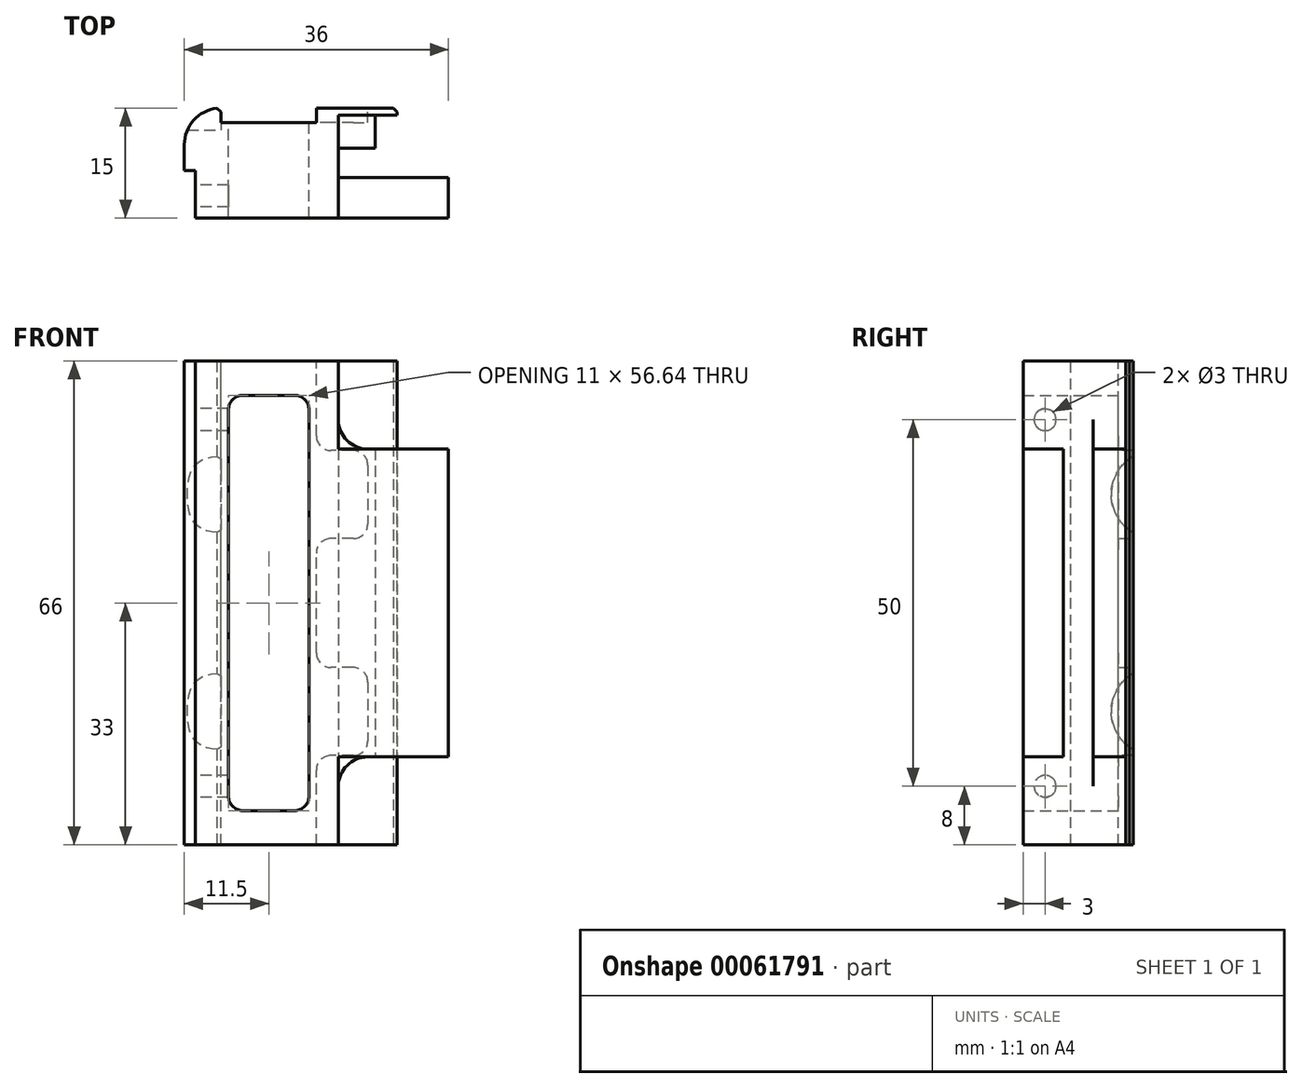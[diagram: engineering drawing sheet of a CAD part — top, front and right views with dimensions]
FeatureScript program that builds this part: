
annotation { "Feature Type Name" : "Feature", "Feature Type Description" : "" }
export const myFeature = defineFeature(function(context is Context, id is Id, definition is map)
    precondition{}
    {
        {
            var Q0;
            Q0=qCreatedBy(makeId("Front.planeOp"),FACE);
            var sketch = newSketch(context, id + "F0", { "sketchPlane" : qUnion([Q0])});
            skLineSegment(sketch, "E0.bottom", {"start": v(5.5, -28.32) * mm, "end": v(-5.5, -28.32) * mm});
            skLineSegment(sketch, "E0.top", {"start": v(5.5, 28.32) * mm, "end": v(-5.5, 28.32) * mm});
            skLineSegment(sketch, "E0.left", {"start": v(5.5, -28.32) * mm, "end": v(5.5, 28.32) * mm});
            skLineSegment(sketch, "E0.right", {"start": v(-5.5, -28.32) * mm, "end": v(-5.5, 28.32) * mm});
            skPoint(sketch, "E0.middle", {"position": v(0, 0) * mm});
            skLineSegment(sketch, "E1.bottom", {"start": v(9.5, -33) * mm, "end": v(-11.5, -33) * mm});
            skLineSegment(sketch, "E1.top", {"start": v(9.5, 33) * mm, "end": v(-11.5, 33) * mm});
            skLineSegment(sketch, "E1.right", {"start": v(-11.5, -33) * mm, "end": v(-11.5, 33) * mm});
            skLineSegment(sketch, "E2", {"start": v(9.5, 33) * mm, "end": v(9.5, -33) * mm});
            skSolve(sketch);
        }
        {
            var Q0;
            Q0 = qSketchRegion(id + "F0", true);
            extrude(context, id + "F1", {"entities" : qUnion([Q0]), "depth" : 15 * mm});
        }
        {
            var Q0;
            Q0=makeQuery(id+"F1.opExtrude","CAP_EDGE",EDGE,{"disambiguationData":[OSD([sQuery(id+"F0.wireOp",EDGE,"E1.right")])],"isStart":true});
            fillet(context, id + "F2", {"entities" : qUnion([Q0]), "radius" : 5 * mm, "tangentPropagation" : true, "allowEdgeOverflow" : false});
        }
        {
            var Q0;
            Q0=qCreatedBy(makeId("Front.planeOp"),FACE);
            var sketch = newSketch(context, id + "F3", { "sketchPlane" : qUnion([Q0])});
            skLineSegment(sketch, "E3.bottom", {"start": v(9.5, -21) * mm, "end": v(24.5, -21) * mm});
            skLineSegment(sketch, "E3.top", {"start": v(9.5, 21) * mm, "end": v(24.5, 21) * mm});
            skLineSegment(sketch, "E3.left", {"start": v(9.5, -21) * mm, "end": v(9.5, 21) * mm});
            skLineSegment(sketch, "E3.right", {"start": v(24.5, -21) * mm, "end": v(24.5, 21) * mm});
            skPoint(sketch, "E3.middle", {"position": v(17, 0) * mm});
            skSolve(sketch);
        }
        {
            var Q0;
            Q0=makeQuery(id+"F3.imprint","IMPRINT",FACE,{"disambiguationData":[TD([[makeQuery(id+"F3.imprint","IMPRINT",EDGE,{"derivedFrom":sQuery(id+"F3.wireOp",EDGE,"E3.bottom")}),1.0]])]});
            extrude(context, id + "F4", {"entities" : qUnion([Q0]), "operationType" : NewBodyOperationType.ADD, "depth" : 15 * mm, "hasSecondDirection" : true, "secondDirectionOppositeDirection" : false, "secondDirectionDepth" : 9.5 * mm});
        }
        {
            var Q0;
            Q0=makeQuery(id+"F1.opExtrude","SWEPT_EDGE",EDGE,{"disambiguationData":[OSD([sQuery(id+"F0.wireOp",EDGE,"E0.bottom"),sQuery(id+"F0.wireOp",EDGE,"E0.left")])]});
            var Q1;
            Q1=makeQuery(id+"F1.opExtrude","SWEPT_EDGE",EDGE,{"disambiguationData":[OSD([sQuery(id+"F0.wireOp",EDGE,"E0.bottom"),sQuery(id+"F0.wireOp",EDGE,"E0.right")])]});
            var Q2;
            Q2=makeQuery(id+"F1.opExtrude","SWEPT_EDGE",EDGE,{"disambiguationData":[OSD([sQuery(id+"F0.wireOp",EDGE,"E0.top"),sQuery(id+"F0.wireOp",EDGE,"E0.right")])]});
            var Q3;
            Q3=makeQuery(id+"F1.opExtrude","SWEPT_EDGE",EDGE,{"disambiguationData":[OSD([sQuery(id+"F0.wireOp",EDGE,"E0.top"),sQuery(id+"F0.wireOp",EDGE,"E0.left")])]});
            fillet(context, id + "F5", {"entities" : qUnion([Q0, Q1, Q2, Q3]), "radius" : 2 * mm, "tangentPropagation" : true, "allowEdgeOverflow" : false});
        }
        {
            var Q0;
            Q0=qCreatedBy(makeId("Top.planeOp"),FACE);
            var sketch = newSketch(context, id + "F6", { "sketchPlane" : qUnion([Q0])});
            skLineSegment(sketch, "E4.bottom", {"start": v(-10, -15) * mm, "end": v(-11.5, -15) * mm});
            skLineSegment(sketch, "E4.top", {"start": v(-10, -8.5) * mm, "end": v(-11.5, -8.5) * mm});
            skLineSegment(sketch, "E4.left", {"start": v(-10, -15) * mm, "end": v(-10, -8.5) * mm});
            skLineSegment(sketch, "E4.right", {"start": v(-11.5, -15) * mm, "end": v(-11.5, -8.5) * mm});
            skSolve(sketch);
        }
        {
            var Q0;
            Q0 = qSketchRegion(id + "F6", true);
            extrude(context, id + "F7", {"entities" : qUnion([Q0]), "operationType" : NewBodyOperationType.REMOVE, "oppositeDirection" : true, "depth" : 50 * mm, "hasSecondDirection" : true, "secondDirectionOppositeDirection" : false, "secondDirectionDepth" : 50 * mm});
        }
        {
            var Q0;
            Q0=makeQuery(id+"F7.boolean.opBoolean","COPY",FACE,{"derivedFrom":makeQuery(id+"F7.opExtrude","SWEPT_FACE",FACE,{"disambiguationData":[OSD([sQuery(id+"F6.wireOp",EDGE,"E4.left")])]})});
            var sketch = newSketch(context, id + "F8", { "sketchPlane" : qUnion([Q0])});
            skCircle(sketch, "E5", {"center": v(12, 25) * mm, "radius": 1.5 * mm});
            skCircle(sketch, "E6", {"center": v(12, -25) * mm, "radius": 1.5 * mm});
            skSolve(sketch);
        }
        {
            var Q0;
            Q0 = qSketchRegion(id + "F8", true);
            extrude(context, id + "F9", {"entities" : qUnion([Q0]), "operationType" : NewBodyOperationType.REMOVE, "oppositeDirection" : true, "depth" : 5 * mm});
        }
        {
            var Q0;
            Q0=qCreatedBy(makeId("Top.planeOp"),FACE);
            var sketch = newSketch(context, id + "F10", { "sketchPlane" : qUnion([Q0])});
            skLineSegment(sketch, "E7.bottom", {"start": v(17.5, -1) * mm, "end": v(14.5, -1) * mm});
            skLineSegment(sketch, "E7.top", {"start": v(17.5, 0) * mm, "end": v(14.5, 0) * mm});
            skLineSegment(sketch, "E7.left", {"start": v(17.5, -1) * mm, "end": v(17.5, 0) * mm});
            skLineSegment(sketch, "E7.right", {"start": v(14.5, -1) * mm, "end": v(14.5, 0) * mm});
            skLineSegment(sketch, "E8.bottom", {"start": v(9.5, 0) * mm, "end": v(14.5, 0) * mm});
            skLineSegment(sketch, "E8.top", {"start": v(9.5, -5.45) * mm, "end": v(14.5, -5.45) * mm});
            skLineSegment(sketch, "E8.left", {"start": v(9.5, 0) * mm, "end": v(9.5, -5.45) * mm});
            skLineSegment(sketch, "E8.right", {"start": v(14.5, 0) * mm, "end": v(14.5, -5.45) * mm});
            skSolve(sketch);
        }
        {
            var Q0;
            Q0=makeQuery(id+"F10.imprint","IMPRINT",FACE,{"disambiguationData":[TD([[makeQuery(id+"F10.imprint","IMPRINT",EDGE,{"derivedFrom":sQuery(id+"F10.wireOp",EDGE,"E7.bottom")}),-1.0]])]});
            var Q1;
            {var subQ2=sQuery(id+"F10.wireOp",EDGE,"E8.bottom");Q1=makeQuery(id+"F10.imprint","IMPRINT",FACE,{"disambiguationData":[TD([[makeQuery(id+"F10.imprint","IMPRINT",EDGE,{"derivedFrom":subQ2}),-1.0]])]});}
            extrude(context, id + "F11", {"entities" : qUnion([Q0, Q1]), "operationType" : NewBodyOperationType.ADD, "depth" : 33 * mm, "hasSecondDirection" : true, "secondDirectionOppositeDirection" : true, "secondDirectionDepth" : 33 * mm});
        }
        {
            var Q0;
            Q0=makeQuery(id+"F11.opExtrude","SWEPT_EDGE",EDGE,{"disambiguationData":[OSD([sQuery(id+"F10.wireOp",EDGE,"E7.top"),sQuery(id+"F10.wireOp",EDGE,"E7.left")])]});
            chamfer(context, id + "F12", {"entities" : qUnion([Q0]), "width" : 0.5 * mm, "tangentPropagation" : true});
        }
        {
            var Q0;
            Q0=makeQuery(id+"F4.boolean.opBoolean","MERGE",FACE,{"derivedFrom":[makeQuery(id+"F1.opExtrude","CAP_FACE",FACE,{"disambiguationData":[OSD([sQuery(id+"F0.wireOp",EDGE,"E0.bottom"),sQuery(id+"F0.wireOp",EDGE,"E0.top"),sQuery(id+"F0.wireOp",EDGE,"E0.left"),sQuery(id+"F0.wireOp",EDGE,"E0.right"),sQuery(id+"F0.wireOp",EDGE,"E1.bottom"),sQuery(id+"F0.wireOp",EDGE,"E1.top"),sQuery(id+"F0.wireOp",EDGE,"E1.right"),sQuery(id+"F0.wireOp",EDGE,"E2")])],"isStart":false}),makeQuery(id+"F4.opExtrude","CAP_FACE",FACE,{"disambiguationData":[OSD([sQuery(id+"F3.wireOp",EDGE,"E3.bottom"),sQuery(id+"F3.wireOp",EDGE,"E3.top"),sQuery(id+"F3.wireOp",EDGE,"E3.left"),sQuery(id+"F3.wireOp",EDGE,"E3.right")])],"isStart":false})]});
            var sketch = newSketch(context, id + "F13", { "sketchPlane" : qUnion([Q0])});
            skLineSegment(sketch, "E9.bottom", {"start": v(9.5, -33) * mm, "end": v(14.5, -33) * mm});
            skLineSegment(sketch, "E9.top", {"start": v(9.5, -21) * mm, "end": v(14.5, -21) * mm});
            skLineSegment(sketch, "E9.left", {"start": v(9.5, -33) * mm, "end": v(9.5, -21) * mm});
            skLineSegment(sketch, "E9.right", {"start": v(14.5, -33) * mm, "end": v(14.5, -21) * mm});
            skLineSegment(sketch, "E10.bottom", {"start": v(9.5, 33) * mm, "end": v(14.5, 33) * mm});
            skLineSegment(sketch, "E10.top", {"start": v(9.5, 21) * mm, "end": v(14.5, 21) * mm});
            skLineSegment(sketch, "E10.left", {"start": v(9.5, 33) * mm, "end": v(9.5, 21) * mm});
            skLineSegment(sketch, "E10.right", {"start": v(14.5, 33) * mm, "end": v(14.5, 21) * mm});
            skSolve(sketch);
        }
        {
            var Q0;
            Q0 = qSketchRegion(id + "F13", true);
            extrude(context, id + "F14", {"entities" : qUnion([Q0]), "operationType" : NewBodyOperationType.REMOVE, "oppositeDirection" : true, "depth" : 14 * mm});
        }
        {
            var Q0;
            Q0=makeQuery(id+"F14.boolean.opBoolean","COPY",EDGE,{"derivedFrom":makeQuery(id+"F14.opExtrude","SWEPT_EDGE",EDGE,{"disambiguationData":[OSD([sQuery(id+"F13.wireOp",EDGE,"E9.top"),sQuery(id+"F13.wireOp",EDGE,"E9.left")])]})});
            var Q1;
            Q1=makeQuery(id+"F14.boolean.opBoolean","COPY",EDGE,{"derivedFrom":makeQuery(id+"F14.opExtrude","SWEPT_EDGE",EDGE,{"disambiguationData":[OSD([sQuery(id+"F13.wireOp",EDGE,"E10.top"),sQuery(id+"F13.wireOp",EDGE,"E10.left")])]})});
            var Q2;
            Q2=makeQuery(id+"F4.opExtrude","SWEPT_EDGE",EDGE,{"disambiguationData":[OSD([sQuery(id+"F3.wireOp",EDGE,"E3.top"),sQuery(id+"F3.wireOp",EDGE,"E3.left")])]});
            var Q3;
            Q3=makeQuery(id+"F4.opExtrude","SWEPT_EDGE",EDGE,{"disambiguationData":[OSD([sQuery(id+"F3.wireOp",EDGE,"E3.bottom"),sQuery(id+"F3.wireOp",EDGE,"E3.left")])]});
            fillet(context, id + "F15", {"entities" : qUnion([Q0, Q1, Q2, Q3]), "radius" : 4 * mm, "tangentPropagation" : true, "allowEdgeOverflow" : false});
        }
        {
            var Q0;
            Q0=qCreatedBy(makeId("Front.planeOp"),FACE);
            var sketch = newSketch(context, id + "F16", { "sketchPlane" : qUnion([Q0])});
            skLineSegment(sketch, "E11.bottom", {"start": v(-6.5, -35) * mm, "end": v(6.5, -35) * mm});
            skLineSegment(sketch, "E11.top", {"start": v(-6.5, 35) * mm, "end": v(6.5, 35) * mm});
            skLineSegment(sketch, "E11.left", {"start": v(-6.5, -35) * mm, "end": v(-6.5, 35) * mm});
            skLineSegment(sketch, "E11.right", {"start": v(6.5, -35) * mm, "end": v(6.5, 35) * mm});
            skPoint(sketch, "E11.middle", {"position": v(0, 0) * mm});
            skSolve(sketch);
        }
        {
            var Q0;
            Q0=makeQuery(id+"F16.imprint","IMPRINT",FACE,{"disambiguationData":[TD([[makeQuery(id+"F16.imprint","IMPRINT",EDGE,{"derivedFrom":sQuery(id+"F16.wireOp",EDGE,"E11.bottom")}),1.0]])]});
            extrude(context, id + "F17", {"entities" : qUnion([Q0]), "operationType" : NewBodyOperationType.REMOVE, "depth" : 2 * mm});
        }
        {
            var Q0;
            Q0=makeQuery(id+"F11.boolean.opBoolean","MERGE",FACE,{"derivedFrom":[makeQuery(id+"F1.opExtrude","CAP_FACE",FACE,{"disambiguationData":[OSD([sQuery(id+"F0.wireOp",EDGE,"E0.bottom"),sQuery(id+"F0.wireOp",EDGE,"E0.top"),sQuery(id+"F0.wireOp",EDGE,"E0.left"),sQuery(id+"F0.wireOp",EDGE,"E0.right"),sQuery(id+"F0.wireOp",EDGE,"E1.bottom"),sQuery(id+"F0.wireOp",EDGE,"E1.top"),sQuery(id+"F0.wireOp",EDGE,"E1.right"),sQuery(id+"F0.wireOp",EDGE,"E2")])],"isStart":true}),makeQuery(id+"F11.opExtrude","SWEPT_FACE",FACE,{"disambiguationData":[OSD([sQuery(id+"F10.wireOp",EDGE,"E7.top"),sQuery(id+"F10.wireOp",EDGE,"E8.bottom")])]})]});
            var sketch = newSketch(context, id + "F18", { "sketchPlane" : qUnion([Q0])});
            skLineSegment(sketch, "E12.bottom", {"start": v(-13.5, 20.8) * mm, "end": v(6.5, 20.8) * mm});
            skLineSegment(sketch, "E12.top", {"start": v(-13.5, 8.8) * mm, "end": v(6.5, 8.8) * mm});
            skLineSegment(sketch, "E12.left", {"start": v(-13.5, 20.8) * mm, "end": v(-13.5, 8.8) * mm});
            skLineSegment(sketch, "E12.right", {"start": v(6.5, 20.8) * mm, "end": v(6.5, 8.8) * mm});
            skPoint(sketch, "E12.middle", {"position": v(-3.5, 14.8) * mm});
            skLineSegment(sketch, "E13.bottom", {"start": v(-13.5, -8.8) * mm, "end": v(6.5, -8.8) * mm});
            skLineSegment(sketch, "E13.top", {"start": v(-13.5, -20.8) * mm, "end": v(6.5, -20.8) * mm});
            skLineSegment(sketch, "E13.left", {"start": v(-13.5, -8.8) * mm, "end": v(-13.5, -20.8) * mm});
            skLineSegment(sketch, "E13.right", {"start": v(6.5, -8.8) * mm, "end": v(6.5, -20.8) * mm});
            skPoint(sketch, "E13.middle", {"position": v(-3.5, -14.8) * mm});
            skSolve(sketch);
        }
        {
            var Q0;
            Q0 = qSketchRegion(id + "F18", true);
            extrude(context, id + "F19", {"entities" : qUnion([Q0]), "operationType" : NewBodyOperationType.REMOVE, "oppositeDirection" : true, "depth" : 2 * mm});
        }
        {
            var Q0;
            Q0=makeQuery(id+"F19.boolean.opBoolean","COPY",EDGE,{"derivedFrom":makeQuery(id+"F19.opExtrude","SWEPT_EDGE",EDGE,{"disambiguationData":[OSD([sQuery(id+"F18.wireOp",EDGE,"E13.top"),sQuery(id+"F18.wireOp",EDGE,"E13.left")])]})});
            var Q1;
            Q1=makeQuery(id+"F19.boolean.opBoolean","COPY",EDGE,{"derivedFrom":makeQuery(id+"F19.opExtrude","SWEPT_EDGE",EDGE,{"disambiguationData":[OSD([sQuery(id+"F18.wireOp",EDGE,"E12.bottom"),sQuery(id+"F18.wireOp",EDGE,"E12.left")])]})});
            var Q2;
            Q2=makeQuery(id+"F19.boolean.opBoolean","INTERSECT",EDGE,{"derivedFrom":[makeQuery(id+"F17.boolean.opBoolean","COPY",FACE,{"derivedFrom":makeQuery(id+"F17.opExtrude","SWEPT_FACE",FACE,{"disambiguationData":[OSD([sQuery(id+"F16.wireOp",EDGE,"E11.right")])]})}),makeQuery(id+"F19.opExtrude","SWEPT_FACE",FACE,{"disambiguationData":[OSD([sQuery(id+"F18.wireOp",EDGE,"E12.bottom")])]})]});
            var Q3;
            Q3=makeQuery(id+"F19.boolean.opBoolean","INTERSECT",EDGE,{"derivedFrom":[makeQuery(id+"F17.boolean.opBoolean","COPY",FACE,{"derivedFrom":makeQuery(id+"F17.opExtrude","SWEPT_FACE",FACE,{"disambiguationData":[OSD([sQuery(id+"F16.wireOp",EDGE,"E11.right")])]})}),makeQuery(id+"F19.opExtrude","SWEPT_FACE",FACE,{"disambiguationData":[OSD([sQuery(id+"F18.wireOp",EDGE,"E12.top")])]})]});
            var Q4;
            Q4=makeQuery(id+"F19.boolean.opBoolean","INTERSECT",EDGE,{"derivedFrom":[makeQuery(id+"F17.boolean.opBoolean","COPY",FACE,{"derivedFrom":makeQuery(id+"F17.opExtrude","SWEPT_FACE",FACE,{"disambiguationData":[OSD([sQuery(id+"F16.wireOp",EDGE,"E11.right")])]})}),makeQuery(id+"F19.opExtrude","SWEPT_FACE",FACE,{"disambiguationData":[OSD([sQuery(id+"F18.wireOp",EDGE,"E13.bottom")])]})]});
            var Q5;
            Q5=makeQuery(id+"F19.boolean.opBoolean","INTERSECT",EDGE,{"derivedFrom":[makeQuery(id+"F17.boolean.opBoolean","COPY",FACE,{"derivedFrom":makeQuery(id+"F17.opExtrude","SWEPT_FACE",FACE,{"disambiguationData":[OSD([sQuery(id+"F16.wireOp",EDGE,"E11.right")])]})}),makeQuery(id+"F19.opExtrude","SWEPT_FACE",FACE,{"disambiguationData":[OSD([sQuery(id+"F18.wireOp",EDGE,"E13.top")])]})]});
            var Q6;
            Q6=makeQuery(id+"F19.boolean.opBoolean","COPY",EDGE,{"derivedFrom":makeQuery(id+"F19.opExtrude","SWEPT_EDGE",EDGE,{"disambiguationData":[OSD([sQuery(id+"F18.wireOp",EDGE,"E13.bottom"),sQuery(id+"F18.wireOp",EDGE,"E13.left")])]})});
            var Q7;
            Q7=makeQuery(id+"F19.boolean.opBoolean","COPY",EDGE,{"derivedFrom":makeQuery(id+"F19.opExtrude","SWEPT_EDGE",EDGE,{"disambiguationData":[OSD([sQuery(id+"F18.wireOp",EDGE,"E12.top"),sQuery(id+"F18.wireOp",EDGE,"E12.left")])]})});
            fillet(context, id + "F20", {"entities" : qUnion([Q0, Q1, Q2, Q3, Q4, Q5, Q6, Q7]), "radius" : 2 * mm, "tangentPropagation" : true, "allowEdgeOverflow" : false});
        }
        {
            var Q0;
            {var subQ0=sQuery(id+"F0.wireOp",EDGE,"E1.right");Q0=makeQuery(id+"F17.boolean.opBoolean","MERGE",EDGE,{"derivedFrom":[makeQuery(id+"F2.opFillet","BLEND_EDGE",EDGE,{"blendedFrom":[makeQuery(id+"F1.opExtrude","CAP_EDGE",EDGE,{"disambiguationData":[OSD([subQ0])],"isStart":true}),makeQuery(id+"F1.opExtrude","CAP_FACE",FACE,{"disambiguationData":[OSD([sQuery(id+"F0.wireOp",EDGE,"E0.bottom"),sQuery(id+"F0.wireOp",EDGE,"E0.top"),sQuery(id+"F0.wireOp",EDGE,"E0.left"),sQuery(id+"F0.wireOp",EDGE,"E0.right"),sQuery(id+"F0.wireOp",EDGE,"E1.bottom"),sQuery(id+"F0.wireOp",EDGE,"E1.top"),subQ0,sQuery(id+"F0.wireOp",EDGE,"E2")])],"isStart":true})],"blendedInto":[makeQuery(id+"F1.opExtrude","CAP_FACE",FACE,{"disambiguationData":[OSD([sQuery(id+"F0.wireOp",EDGE,"E0.bottom"),sQuery(id+"F0.wireOp",EDGE,"E0.top"),sQuery(id+"F0.wireOp",EDGE,"E0.left"),sQuery(id+"F0.wireOp",EDGE,"E0.right"),sQuery(id+"F0.wireOp",EDGE,"E1.bottom"),sQuery(id+"F0.wireOp",EDGE,"E1.top"),subQ0,sQuery(id+"F0.wireOp",EDGE,"E2")])],"isStart":true})]}),makeQuery(id+"F17.opExtrude","CAP_EDGE",EDGE,{"disambiguationData":[OSD([sQuery(id+"F16.wireOp",EDGE,"E11.left")])],"isStart":true})]});}
            var Q1;
            {var subQ2=sQuery(id+"F0.wireOp",EDGE,"E1.bottom");var subQ3=sQuery(id+"F16.wireOp",EDGE,"E11.right");Q1=makeQuery(id+"F19.boolean.opBoolean","SPLIT",EDGE,{"disambiguationData":[TD([makeQuery(id+"F1.opExtrude","SWEPT_FACE",FACE,{"disambiguationData":[OSD([subQ2])]})])],"derivedFrom":makeQuery(id+"F17.boolean.opBoolean","COPY",EDGE,{"derivedFrom":makeQuery(id+"F17.opExtrude","CAP_EDGE",EDGE,{"disambiguationData":[OSD([subQ3])],"isStart":true})})});}
            chamfer(context, id + "F21", {"entities" : qUnion([Q0, Q1]), "width" : 0.5 * mm, "tangentPropagation" : true});
        }
        {
            var Q0;
            Q0=qCreatedBy(makeId("Right.planeOp"),FACE);
            var sketch = newSketch(context, id + "F22", { "sketchPlane" : qUnion([Q0])});
            skCircle(sketch, "E14", {"center": v(3, -14.8) * mm, "radius": 6 * mm});
            skCircle(sketch, "E15", {"center": v(3, 14.8) * mm, "radius": 6 * mm});
            skLineSegment(sketch, "E16", {"start": v(3, -14.8) * mm, "end": v(3, 14.8) * mm, "construction": true});
            skSolve(sketch);
        }
        {
            var Q0;
            Q0 = qSketchRegion(id + "F22", true);
            extrude(context, id + "F23", {"entities" : qUnion([Q0]), "operationType" : NewBodyOperationType.REMOVE, "endBound" : BoundingType.THROUGH_ALL, "oppositeDirection" : true, "depth" : 25 * mm, "hasSecondDirection" : true, "secondDirectionOppositeDirection" : true, "secondDirectionDepth" : 6.5 * mm});
        }
    });
